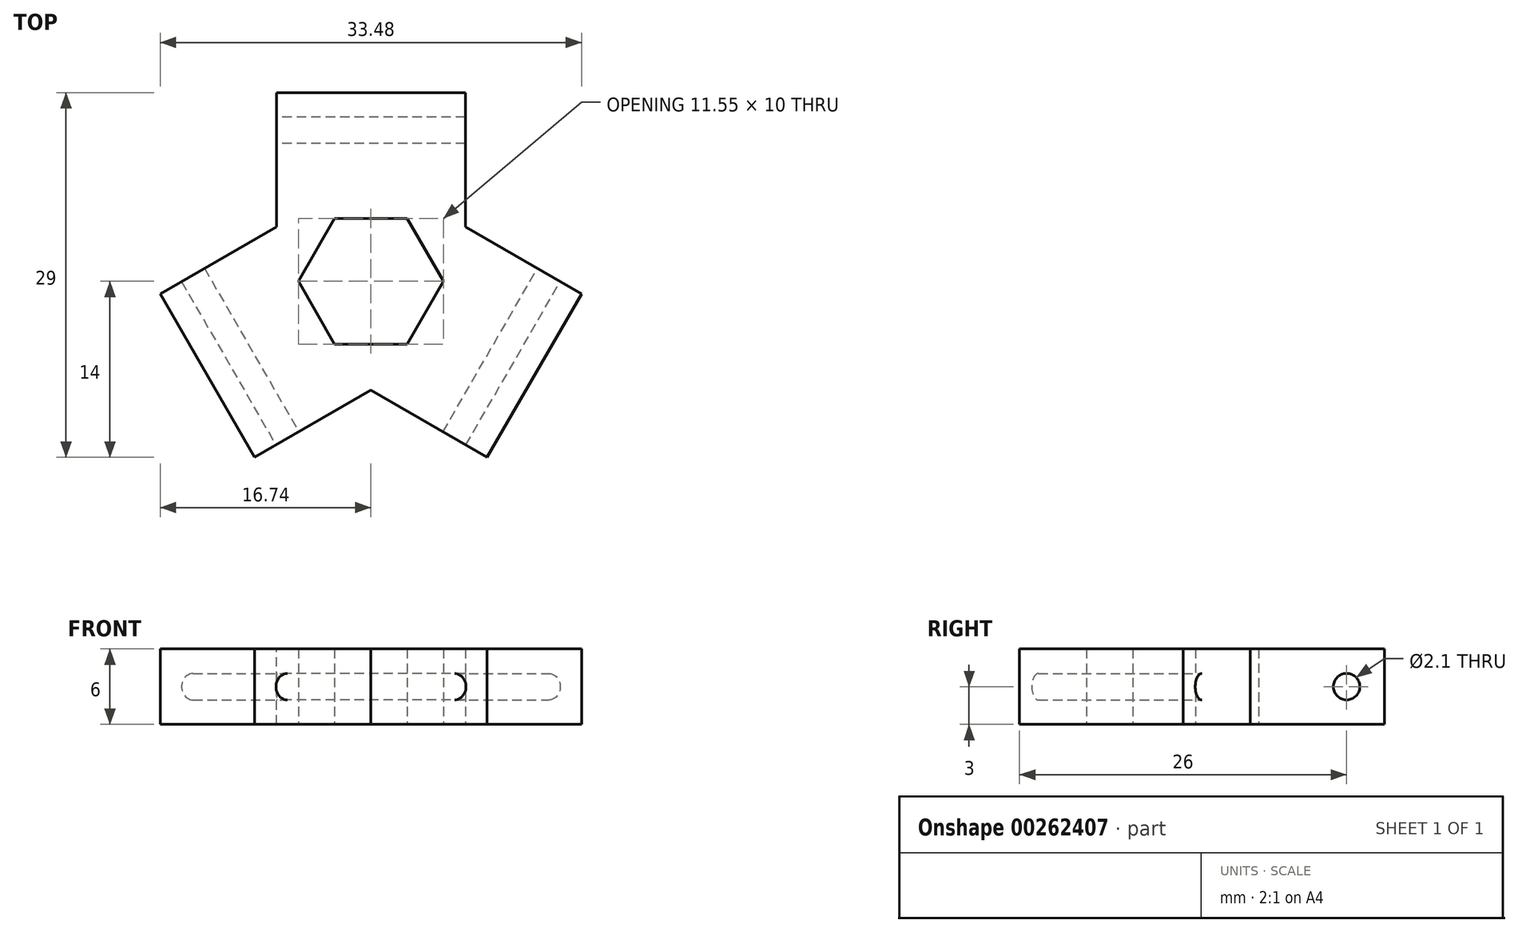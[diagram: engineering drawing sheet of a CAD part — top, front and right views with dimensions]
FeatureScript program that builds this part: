
annotation { "Feature Type Name" : "Feature", "Feature Type Description" : "" }
export const myFeature = defineFeature(function(context is Context, id is Id, definition is map)
    precondition{}
    {
        {
            var Q0;
            Q0=qCreatedBy(makeId("Top.planeOp"),FACE);
            var sketch = newSketch(context, id + "F0", { "sketchPlane" : qUnion([Q0])});
            skLineSegment(sketch, "E0.bottom", {"start": v(-7.5, 0) * mm, "end": v(7.5, 0) * mm});
            skLineSegment(sketch, "E0.top", {"start": v(-7.5, 15) * mm, "end": v(7.5, 15) * mm});
            skLineSegment(sketch, "E0.left", {"start": v(-7.5, 0) * mm, "end": v(-7.5, 15) * mm});
            skLineSegment(sketch, "E0.right", {"start": v(7.5, 0) * mm, "end": v(7.5, 15) * mm});
            skSolve(sketch);
        }
        {
            var Q0;
            Q0 = qSketchRegion(id + "F0", true);
            extrude(context, id + "F1", {"entities" : qUnion([Q0]), "depth" : 6 * mm});
        }
        {
            var Q0;
            Q0=makeQuery(id+"F1.opExtrude","SWEPT_FACE",FACE,{"disambiguationData":[OSD([sQuery(id+"F0.wireOp",EDGE,"E0.left")])]});
            var sketch = newSketch(context, id + "F2", { "sketchPlane" : qUnion([Q0])});
            skPoint(sketch, "E1", {"position": v(-15, 3) * mm});
            skPoint(sketch, "E2", {"position": v(-12, 0) * mm});
            skCircle(sketch, "E3", {"center": v(-12, 3) * mm, "radius": 1.05 * mm});
            skSolve(sketch);
        }
        {
            var Q0;
            Q0=makeQuery(id+"F2.imprint","IMPRINT",FACE,{"disambiguationData":[TD([[makeQuery(id+"F2.imprint","IMPRINT",EDGE,{"derivedFrom":sQuery(id+"F2.wireOp",EDGE,"E3")}),1.0]])]});
            var Q1;
            Q1=makeQuery(id+"F1.opExtrude","SWEPT_FACE",FACE,{"disambiguationData":[OSD([sQuery(id+"F0.wireOp",EDGE,"E0.right")])]});
            extrude(context, id + "F3", {"entities" : qUnion([Q0]), "operationType" : NewBodyOperationType.REMOVE, "endBound" : BoundingType.UP_TO_SURFACE, "oppositeDirection" : true, "endBoundEntityFace" : qUnion([Q1]), "depth" : 25 * mm});
        }
        {
            var Q0;
            Q0=qCreatedBy(makeId("Front.planeOp"),FACE);
            var sketch = newSketch(context, id + "F4", { "sketchPlane" : qUnion([Q0])});
            skLineSegment(sketch, "E4", {"start": v(0, 24.12) * mm, "end": v(0, -26.86) * mm, "construction": true});
            skSolve(sketch);
        }
        {
            var Q0;
            Q0=makeQuery(id+"F1.opExtrude","SWEPT_BODY",BODY,{"disambiguationData":[OSD([sQuery(id+"F0.wireOp",EDGE,"E0.bottom"),sQuery(id+"F0.wireOp",EDGE,"E0.top"),sQuery(id+"F0.wireOp",EDGE,"E0.left"),sQuery(id+"F0.wireOp",EDGE,"E0.right")])]});
            var Q1;
            Q1=sQuery(id+"F4.wireOp",EDGE,"E4");
            circularPattern(context, id + "F5", {"operationType" : NewBodyOperationType.ADD, "entities" : qUnion([Q0]), "axis" : qUnion([Q1]), "angle" : 360 * degree, "instanceCount" : 3, "equalSpace" : true});
        }
        {
            var Q0;
            Q0=qCreatedBy(makeId("Top.planeOp"),FACE);
            var sketch = newSketch(context, id + "F6", { "sketchPlane" : qUnion([Q0])});
            skCircle(sketch, "E5.cCircle", {"center": v(0, 0) * mm, "radius": 5 * mm, "construction": true});
            skLineSegment(sketch, "E5.0", {"start": v(-2.89, 5) * mm, "end": v(2.89, 5) * mm});
            skLineSegment(sketch, "E5.1", {"start": v(2.89, 5) * mm, "end": v(5.77, 0) * mm});
            skLineSegment(sketch, "E5.2", {"start": v(5.77, 0) * mm, "end": v(2.89, -5) * mm});
            skLineSegment(sketch, "E5.3", {"start": v(2.89, -5) * mm, "end": v(-2.89, -5) * mm});
            skLineSegment(sketch, "E5.4", {"start": v(-2.89, -5) * mm, "end": v(-5.77, 0) * mm});
            skLineSegment(sketch, "E5.5", {"start": v(-5.77, 0) * mm, "end": v(-2.89, 5) * mm});
            skPoint(sketch, "E5.0.midPoint", {"position": v(0, 5) * mm});
            skSolve(sketch);
        }
        {
            var Q0;
            Q0=makeQuery(id+"F6.imprint","IMPRINT",FACE,{"disambiguationData":[TD([[makeQuery(id+"F6.imprint","IMPRINT",EDGE,{"derivedFrom":sQuery(id+"F6.wireOp",EDGE,"E5.0")}),-1.0]])]});
            var Q1;
            {var subQ0=makeQuery(id+"F1.opExtrude","CAP_FACE",FACE,{"disambiguationData":[OSD([sQuery(id+"F0.wireOp",EDGE,"E0.bottom"),sQuery(id+"F0.wireOp",EDGE,"E0.top"),sQuery(id+"F0.wireOp",EDGE,"E0.left"),sQuery(id+"F0.wireOp",EDGE,"E0.right")])],"isStart":false});Q1=makeQuery(id+"F5.boolean.opBoolean","MERGE",FACE,{"derivedFrom":[subQ0,makeQuery(id+"F5.opPattern","COPY",FACE,{"derivedFrom":subQ0,"instanceName":"1"}),makeQuery(id+"F5.opPattern","COPY",FACE,{"derivedFrom":subQ0,"instanceName":"2"})]});}
            extrude(context, id + "F7", {"entities" : qUnion([Q0]), "operationType" : NewBodyOperationType.REMOVE, "endBound" : BoundingType.UP_TO_SURFACE, "endBoundEntityFace" : qUnion([Q1]), "depth" : 25 * mm});
        }
    });
